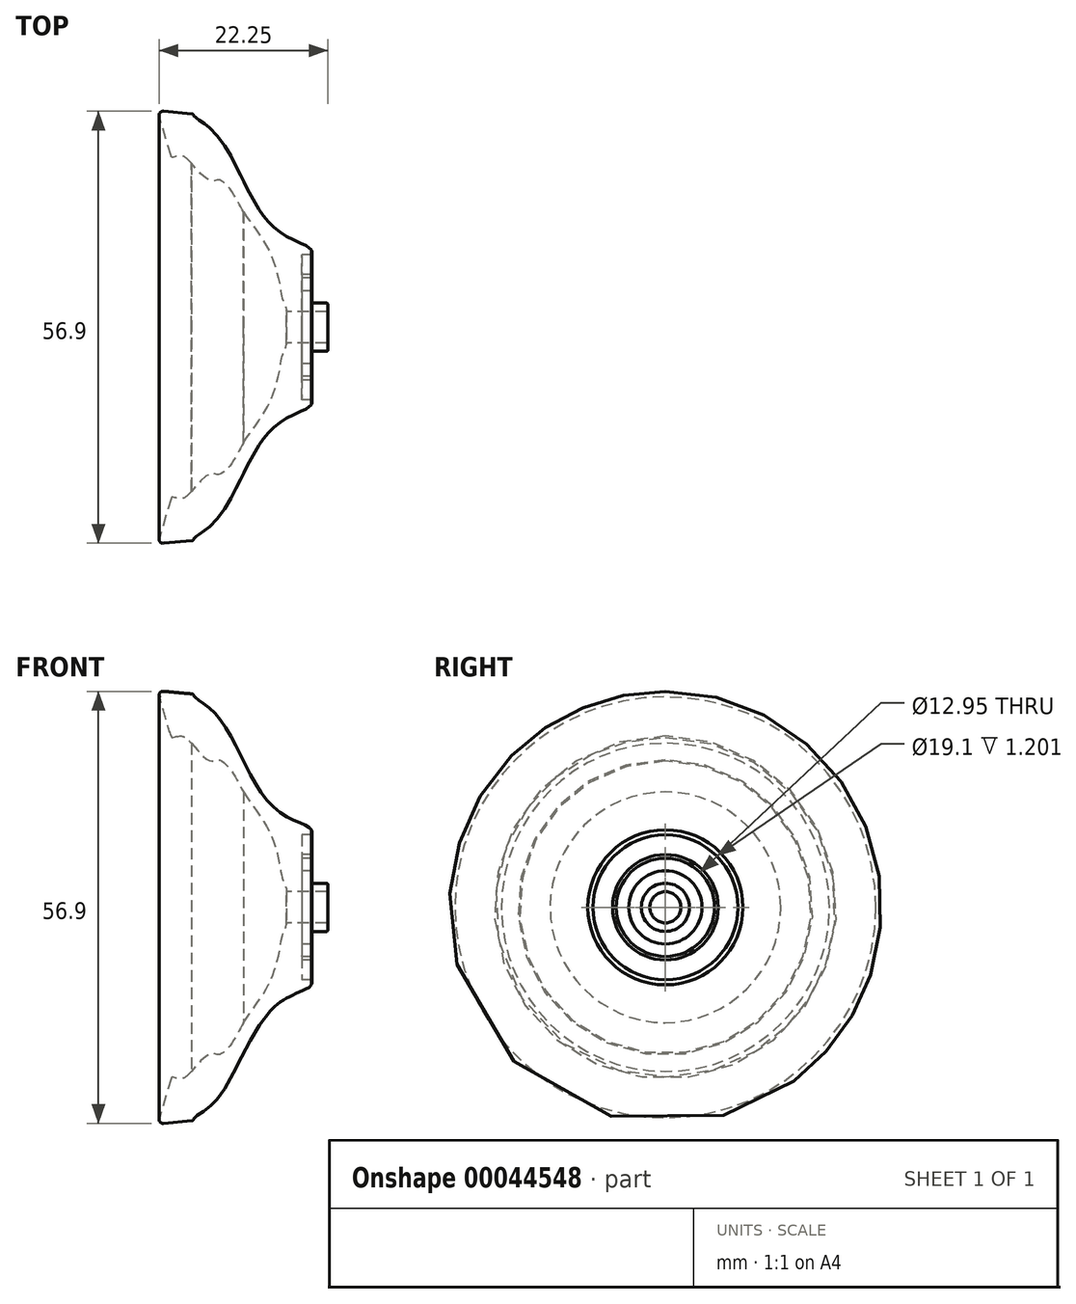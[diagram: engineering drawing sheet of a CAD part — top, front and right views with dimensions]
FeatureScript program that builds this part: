
annotation { "Feature Type Name" : "Feature", "Feature Type Description" : "" }
export const myFeature = defineFeature(function(context is Context, id is Id, definition is map)
    precondition{}
    {
        {
            var Q0;
            Q0=qCreatedBy(makeId("Front.planeOp"),FACE);
            var sketch = newSketch(context, id + "F0", { "sketchPlane" : qUnion([Q0])});
            skLineSegment(sketch, "E0", {"start": v(-27.14, 28.5) * mm, "end": v(36.68, 28.5) * mm, "construction": true});
            skLineSegment(sketch, "E1", {"start": v(20, 42.96) * mm, "end": v(20, -13.53) * mm, "construction": true});
            skLineSegment(sketch, "E2.bottom", {"start": v(22.05, 3.18) * mm, "end": v(20.1, 3.18) * mm});
            skLineSegment(sketch, "E2.left", {"start": v(22.25, 2.98) * mm, "end": v(22.25, 2.25) * mm});
            skLineSegment(sketch, "E3", {"start": v(20, 3.28) * mm, "end": v(20, 4.82) * mm});
            skLineSegment(sketch, "E4", {"start": v(20, 4.82) * mm, "end": v(18.9, 4.82) * mm});
            skLineSegment(sketch, "E5", {"start": v(18.8, 4.92) * mm, "end": v(18.8, 6.38) * mm});
            skLineSegment(sketch, "E6", {"start": v(18.9, 6.48) * mm, "end": v(20, 6.48) * mm});
            skLineSegment(sketch, "E7", {"start": v(20, 6.95) * mm, "end": v(18.8, 6.95) * mm});
            skLineSegment(sketch, "E8", {"start": v(18.8, 6.95) * mm, "end": v(18.8, 9.55) * mm});
            skLineSegment(sketch, "E9", {"start": v(18.8, 9.55) * mm, "end": v(20, 9.55) * mm});
            skLineSegment(sketch, "E10", {"start": v(4.33, 28.1) * mm, "end": v(0.55, 28.45) * mm});
            skLineSegment(sketch, "E11", {"start": v(6.68, 0) * mm, "end": v(6.68, 0) * mm});
            skLineSegment(sketch, "E12", {"start": v(6.68, 0) * mm, "end": v(22.25, 0) * mm});
            skLineSegment(sketch, "E13.top", {"start": v(20.1, 6.48) * mm, "end": v(20.1, 6.48) * mm});
            skLineSegment(sketch, "E13.left", {"start": v(20.1, 6.85) * mm, "end": v(20.1, 6.58) * mm});
            skLineSegment(sketch, "E14.right", {"start": v(20.1, 9.65) * mm, "end": v(20.1, 10.02) * mm});
            skPoint(sketch, "E15.visualSharp", {"position": v(0, 28.5) * mm});
            skArc(sketch, "E15.filletArc", {"start": v(0.55, 28.45) * mm, "mid": v(0.08, 28.23) * mm, "end": v(0.06, 27.72) * mm});
            skPoint(sketch, "E16.visualSharp", {"position": v(20.1, 10.09) * mm});
            skArc(sketch, "E16.filletArc", {"start": v(20.1, 10.02) * mm, "mid": v(20.1, 10.12) * mm, "end": v(20.07, 10.21) * mm});
            skPoint(sketch, "E17.visualSharp", {"position": v(20.1, 9.55) * mm});
            skArc(sketch, "E17.filletArc", {"start": v(20, 9.55) * mm, "mid": v(20.07, 9.58) * mm, "end": v(20.1, 9.65) * mm});
            skPoint(sketch, "E18.visualSharp", {"position": v(20.1, 6.95) * mm});
            skArc(sketch, "E18.filletArc", {"start": v(20.1, 6.85) * mm, "mid": v(20.07, 6.92) * mm, "end": v(20, 6.95) * mm});
            skPoint(sketch, "E19.visualSharp", {"position": v(20.1, 6.48) * mm});
            skArc(sketch, "E19.filletArc", {"start": v(20, 6.48) * mm, "mid": v(20.07, 6.5) * mm, "end": v(20.1, 6.58) * mm});
            skPoint(sketch, "E20.visualSharp", {"position": v(18.8, 6.48) * mm});
            skArc(sketch, "E20.filletArc", {"start": v(18.9, 6.48) * mm, "mid": v(18.83, 6.45) * mm, "end": v(18.8, 6.38) * mm});
            skPoint(sketch, "E21.visualSharp", {"position": v(18.8, 4.82) * mm});
            skArc(sketch, "E21.filletArc", {"start": v(18.8, 4.92) * mm, "mid": v(18.83, 4.85) * mm, "end": v(18.9, 4.82) * mm});
            skPoint(sketch, "E22.visualSharp", {"position": v(20, 3.18) * mm});
            skArc(sketch, "E22.filletArc", {"start": v(20, 3.28) * mm, "mid": v(20.03, 3.2) * mm, "end": v(20.1, 3.18) * mm});
            skPoint(sketch, "E23.visualSharp", {"position": v(22.25, 3.18) * mm});
            skArc(sketch, "E23.filletArc", {"start": v(22.25, 2.98) * mm, "mid": v(22.2, 3.12) * mm, "end": v(22.05, 3.18) * mm});
            skLineSegment(sketch, "E24", {"start": v(22.05, 2.05) * mm, "end": v(16.9, 2.05) * mm});
            skPoint(sketch, "E25.visualSharp", {"position": v(22.25, 2.05) * mm});
            skArc(sketch, "E25.filletArc", {"start": v(22.05, 2.05) * mm, "mid": v(22.2, 2.1) * mm, "end": v(22.25, 2.25) * mm});
            skPoint(sketch, "E26.visualSharp", {"position": v(6.68, 2.05) * mm});
            skFitSpline(sketch, "E27", {"points": [v(4.56, 28.09) * mm, v(7.35, 25.6) * mm, v(15.06, 13.2) * mm, v(20.07, 10.21) * mm], "startDerivative": vector(-3.1, -6.06) * mm, "endDerivative": vector(3.82, -7.52) * mm});
            skFitSpline(sketch, "E28", {"points": [v(1.64, 22.31) * mm, v(4.26, 21.61) * mm], "startDerivative": vector(5.3, 1.85) * mm, "endDerivative": vector(2.15, -1.96) * mm});
            skLineSegment(sketch, "E29", {"start": v(0.06, 27.72) * mm, "end": v(1.57, 22.56) * mm});
            skArc(sketch, "E30.filletArc", {"start": v(4.54, 27.93) * mm, "mid": v(4.46, 28.05) * mm, "end": v(4.33, 28.1) * mm});
            skArc(sketch, "E31.filletArc", {"start": v(1.57, 22.56) * mm, "mid": v(1.69, 22.4) * mm, "end": v(1.88, 22.39) * mm});
            skFitSpline(sketch, "E32", {"points": [v(4.26, 21.61) * mm, v(7.7, 19.43) * mm, v(9.23, 18.36) * mm, v(11.13, 15.2) * mm], "startDerivative": vector(21.05, -25.85) * mm, "endDerivative": vector(5.63, -9.65) * mm});
            skFitSpline(sketch, "E33", {"points": [v(11.13, 15.2) * mm, v(14.69, 9.65) * mm, v(16.01, 4.85) * mm, v(16.45, 3.14) * mm, v(16.73, 2.05) * mm], "startDerivative": vector(9.73, -15.38) * mm, "endDerivative": vector(-4.18, -3.65) * mm});
            skArc(sketch, "E34.filletArc", {"start": v(16.8, 2.17) * mm, "mid": v(16.82, 2.09) * mm, "end": v(16.9, 2.05) * mm});
            skSolve(sketch);
        }
        {
            var Q0;
            Q0=makeQuery(id+"F0.imprint","IMPRINT",FACE,{"disambiguationData":[TD([[makeQuery(id+"F0.imprint","IMPRINT",EDGE,{"derivedFrom":sQuery(id+"F0.wireOp",EDGE,"E2.bottom")}),1.0]])]});
            var Q1;
            Q1=sQuery(id+"F0.wireOp",EDGE,"E12");
            revolve(context, id + "F1", {"entities" : qUnion([Q0]), "axis" : qUnion([Q1]), "revolveType" : RevolveType.FULL});
        }
    });
